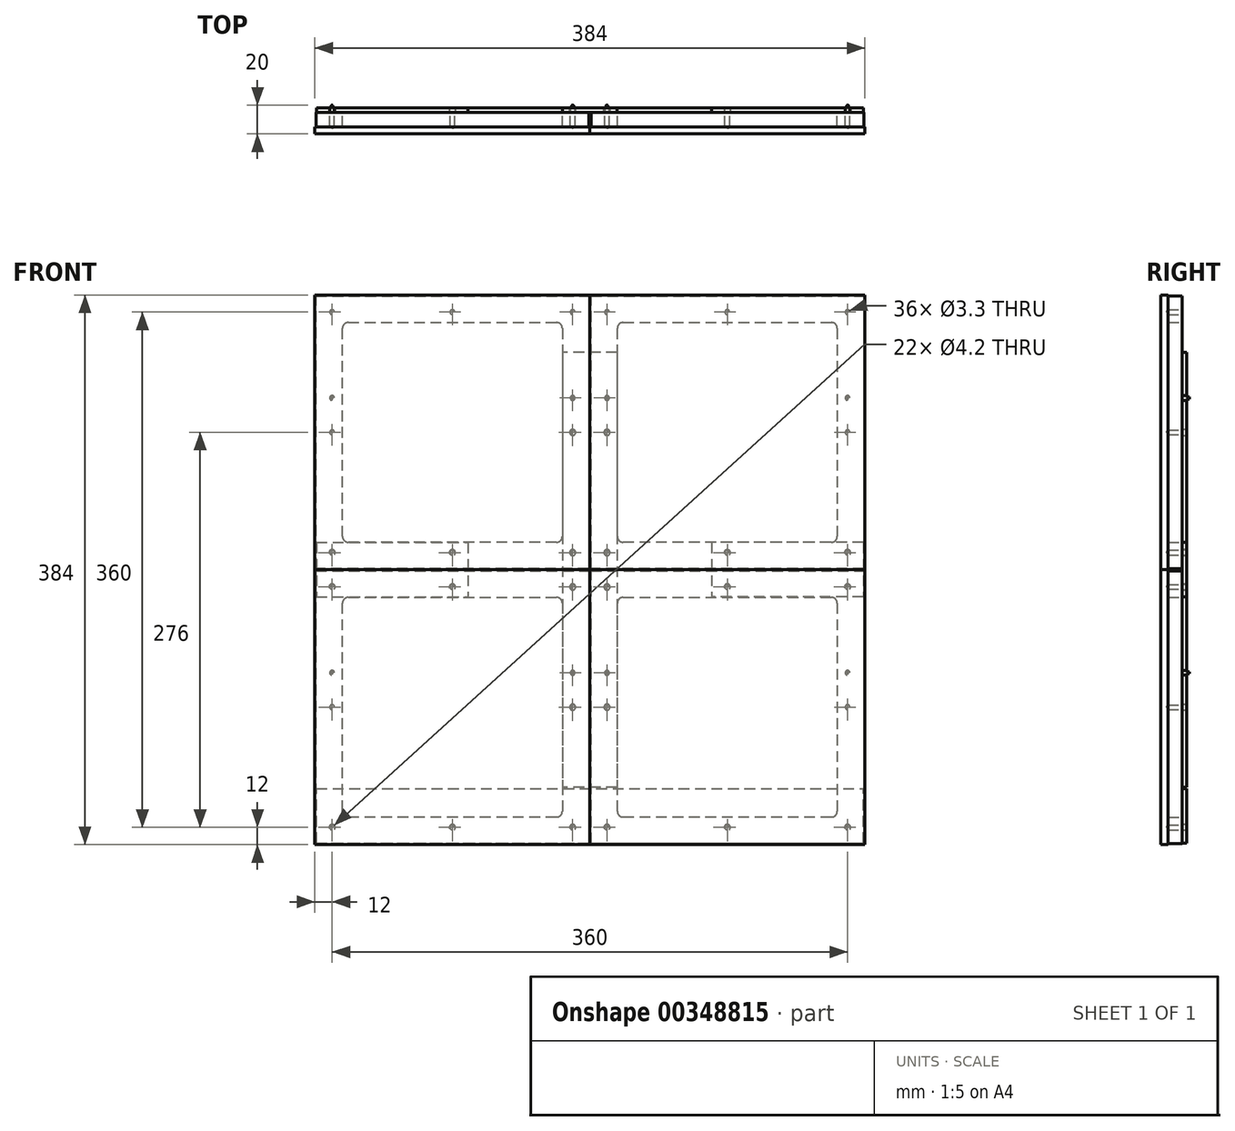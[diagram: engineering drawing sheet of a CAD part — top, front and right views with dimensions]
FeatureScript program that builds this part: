
annotation { "Feature Type Name" : "Feature", "Feature Type Description" : "" }
export const myFeature = defineFeature(function(context is Context, id is Id, definition is map)
    precondition{}
    {
        {
            var Q0;
            Q0=qCreatedBy(makeId("Front.planeOp"),FACE);
            var sketch = newSketch(context, id + "F0", { "sketchPlane" : qUnion([Q0])});
            skLineSegment(sketch, "E0.bottom", {"start": v(-96, -96) * mm, "end": v(96, -96) * mm});
            skLineSegment(sketch, "E0.top", {"start": v(-96, 96) * mm, "end": v(96, 96) * mm});
            skLineSegment(sketch, "E0.left", {"start": v(-96, -96) * mm, "end": v(-96, 96) * mm});
            skLineSegment(sketch, "E0.right", {"start": v(96, -96) * mm, "end": v(96, 96) * mm});
            skPoint(sketch, "E0.middle", {"position": v(0, 0) * mm});
            skSolve(sketch);
        }
        {
            var Q0;
            Q0 = qSketchRegion(id + "F0", true);
            extrude(context, id + "F1", {"entities" : qUnion([Q0]), "depth" : 15 * mm});
        }
        {
            var Q0;
            Q0=qCreatedBy(makeId("Front.planeOp"),FACE);
            var sketch = newSketch(context, id + "F2", { "sketchPlane" : qUnion([Q0])});
            skLineSegment(sketch, "E1.0.0", {"start": v(-96, 96) * mm, "end": v(96, 96) * mm});
            skLineSegment(sketch, "E1.0.1", {"start": v(96, 96) * mm, "end": v(96, -96) * mm});
            skLineSegment(sketch, "E1.0.2", {"start": v(96, -96) * mm, "end": v(-96, -96) * mm});
            skLineSegment(sketch, "E1.0.3", {"start": v(-96, -96) * mm, "end": v(-96, 96) * mm});
            skLineSegment(sketch, "E2.0", {"start": v(-95.25, 95.25) * mm, "end": v(95.25, 95.25) * mm});
            skLineSegment(sketch, "E2.1", {"start": v(-95.25, -95.25) * mm, "end": v(-95.25, 95.25) * mm});
            skLineSegment(sketch, "E2.2", {"start": v(95.25, -95.25) * mm, "end": v(-95.25, -95.25) * mm});
            skLineSegment(sketch, "E2.3", {"start": v(95.25, 95.25) * mm, "end": v(95.25, -95.25) * mm});
            skSolve(sketch);
        }
        {
            var Q0;
            Q0 = qSketchRegion(id + "F2", true);
            extrude(context, id + "F3", {"entities" : qUnion([Q0]), "operationType" : NewBodyOperationType.REMOVE, "depth" : 10 * mm});
        }
        {
            var Q0;
            Q0=makeQuery(id+"F1.opExtrude","CAP_FACE",FACE,{"disambiguationData":[OSD([sQuery(id+"F0.wireOp",EDGE,"E0.bottom"),sQuery(id+"F0.wireOp",EDGE,"E0.top"),sQuery(id+"F0.wireOp",EDGE,"E0.left"),sQuery(id+"F0.wireOp",EDGE,"E0.right")])],"isStart":true});
            var sketch = newSketch(context, id + "F4", { "sketchPlane" : qUnion([Q0])});
            skLineSegment(sketch, "E3.0", {"start": v(72.75, 76.75) * mm, "end": v(-72.75, 76.75) * mm});
            skLineSegment(sketch, "E3.1", {"start": v(76.75, -72.75) * mm, "end": v(76.75, 72.75) * mm});
            skLineSegment(sketch, "E3.2", {"start": v(-72.75, -76.75) * mm, "end": v(72.75, -76.75) * mm});
            skLineSegment(sketch, "E3.3", {"start": v(-76.75, 72.75) * mm, "end": v(-76.75, -72.75) * mm});
            skPoint(sketch, "E4.visualSharp", {"position": v(76.75, 76.75) * mm});
            skArc(sketch, "E4.filletArc", {"start": v(76.75, 72.75) * mm, "mid": v(75.58, 75.58) * mm, "end": v(72.75, 76.75) * mm});
            skPoint(sketch, "E5.visualSharp", {"position": v(76.75, -76.75) * mm});
            skArc(sketch, "E5.filletArc", {"start": v(72.75, -76.75) * mm, "mid": v(75.58, -75.58) * mm, "end": v(76.75, -72.75) * mm});
            skPoint(sketch, "E6.visualSharp", {"position": v(-76.75, -76.75) * mm});
            skArc(sketch, "E6.filletArc", {"start": v(-76.75, -72.75) * mm, "mid": v(-75.58, -75.58) * mm, "end": v(-72.75, -76.75) * mm});
            skPoint(sketch, "E7.visualSharp", {"position": v(-76.75, 76.75) * mm});
            skArc(sketch, "E7.filletArc", {"start": v(-72.75, 76.75) * mm, "mid": v(-75.58, 75.58) * mm, "end": v(-76.75, 72.75) * mm});
            skLineSegment(sketch, "E8.0.0", {"start": v(95.25, 95.25) * mm, "end": v(-95.25, 95.25) * mm, "construction": true});
            skLineSegment(sketch, "E8.0.1", {"start": v(-95.25, 95.25) * mm, "end": v(-95.25, -95.25) * mm, "construction": true});
            skLineSegment(sketch, "E8.0.2", {"start": v(-95.25, -95.25) * mm, "end": v(95.25, -95.25) * mm, "construction": true});
            skLineSegment(sketch, "E8.0.3", {"start": v(95.25, -95.25) * mm, "end": v(95.25, 95.25) * mm, "construction": true});
            skSolve(sketch);
        }
        {
            var Q0;
            Q0=makeQuery(id+"F4.imprint","IMPRINT",FACE,{"disambiguationData":[TD([[makeQuery(id+"F4.imprint","IMPRINT",EDGE,{"derivedFrom":sQuery(id+"F4.wireOp",EDGE,"E3.0")}),1.0]])]});
            extrude(context, id + "F5", {"entities" : qUnion([Q0]), "operationType" : NewBodyOperationType.REMOVE, "oppositeDirection" : true, "depth" : 10 * mm});
        }
        {
            var Q0;
            Q0=makeQuery(id+"F1.opExtrude","CAP_FACE",FACE,{"disambiguationData":[OSD([sQuery(id+"F0.wireOp",EDGE,"E0.bottom"),sQuery(id+"F0.wireOp",EDGE,"E0.top"),sQuery(id+"F0.wireOp",EDGE,"E0.left"),sQuery(id+"F0.wireOp",EDGE,"E0.right")])],"isStart":true});
            var sketch = newSketch(context, id + "F6", { "sketchPlane" : qUnion([Q0])});
            skPoint(sketch, "E9", {"position": v(-84, 84) * mm});
            skPoint(sketch, "E10", {"position": v(0, 84) * mm});
            skPoint(sketch, "E11", {"position": v(84, 84) * mm});
            skPoint(sketch, "E12", {"position": v(84, 0) * mm});
            skPoint(sketch, "E13", {"position": v(84, -84) * mm});
            skPoint(sketch, "E14", {"position": v(0, -84) * mm});
            skPoint(sketch, "E15", {"position": v(-84, -84) * mm});
            skPoint(sketch, "E16", {"position": v(-84, 0) * mm});
            skLineSegment(sketch, "E17", {"start": v(0, 0) * mm, "end": v(95.25, 95.25) * mm, "construction": true});
            skSolve(sketch);
        }
        {
            var Q0;
            Q0=sQuery(id+"F6.wireOp",VERTEX,"E9");
            var Q1;
            Q1=sQuery(id+"F6.wireOp",VERTEX,"E16");
            var Q2;
            Q2=sQuery(id+"F6.wireOp",VERTEX,"E15");
            var Q3;
            Q3=sQuery(id+"F6.wireOp",VERTEX,"E14");
            var Q4;
            Q4=sQuery(id+"F6.wireOp",VERTEX,"E13");
            var Q5;
            Q5=sQuery(id+"F6.wireOp",VERTEX,"E12");
            var Q6;
            Q6=sQuery(id+"F6.wireOp",VERTEX,"E11");
            var Q7;
            Q7=sQuery(id+"F6.wireOp",VERTEX,"E10");
            var Q8;
            Q8=makeQuery(id+"F1.opExtrude","SWEPT_BODY",BODY,{"disambiguationData":[OSD([sQuery(id+"F0.wireOp",EDGE,"E0.bottom"),sQuery(id+"F0.wireOp",EDGE,"E0.top"),sQuery(id+"F0.wireOp",EDGE,"E0.left"),sQuery(id+"F0.wireOp",EDGE,"E0.right")])]});
            hole(context, id + "F7", {"style" : HoleStyle.SIMPLE, "endStyle" : HoleEndStyle.BLIND, "standardTappedOrClearance" : lookupTablePath({ "standard" : "ISO", "engagement" : "75%", "pitch" : "0.7 mm", "size" : "M4", "type" : "Tapped" }), "standardBlindInLast" : lookupTablePath({ "standard" : "ISO", "engagement" : "75%", "pitch" : "0.7 mm", "size" : "M4", "type" : "Tapped" }), "holeDiameter" : 3.3 * mm, "showTappedDepth" : true, "holeDepth" : 10.1 * mm, "tappedDepth" : 8 * mm, "tapClearance" : 3, "locations" : qUnion([Q0, Q1, Q2, Q3, Q4, Q5, Q6, Q7]), "scope" : qUnion([Q8]), "majorDiameter" : 4 * mm});
        }
        {
            var Q0;
            Q0=qCreatedBy(makeId("Front.planeOp"),FACE);
            var sketch = newSketch(context, id + "F8", { "sketchPlane" : qUnion([Q0])});
            skCircle(sketch, "E18", {"center": v(84, 24) * mm, "radius": 1.65 * mm});
            skCircle(sketch, "E19.MirrorC", {"center": v(-84, 24) * mm, "radius": 1.65 * mm});
            skSolve(sketch);
        }
        {
            var Q0;
            Q0 = qSketchRegion(id + "F8", true);
            extrude(context, id + "F9", {"entities" : qUnion([Q0]), "operationType" : NewBodyOperationType.ADD, "oppositeDirection" : true, "depth" : 5 * mm});
        }
        {
            var Q0;
            Q0=makeQuery(id+"F9.opExtrude","CAP_EDGE",EDGE,{"disambiguationData":[OSD([sQuery(id+"F8.wireOp",EDGE,"E18")])],"isStart":false});
            var Q1;
            Q1=makeQuery(id+"F9.opExtrude","CAP_EDGE",EDGE,{"disambiguationData":[OSD([sQuery(id+"F8.wireOp",EDGE,"E19.MirrorC")])],"isStart":false});
            fillet(context, id + "F10", {"entities" : qUnion([Q0, Q1]), "radius" : 1 * mm, "tangentPropagation" : true, "allowEdgeOverflow" : false});
        }
        {
            var Q0;
            Q0=makeQuery(id+"F1.opExtrude","SWEPT_BODY",BODY,{"disambiguationData":[OSD([sQuery(id+"F0.wireOp",EDGE,"E0.bottom"),sQuery(id+"F0.wireOp",EDGE,"E0.top"),sQuery(id+"F0.wireOp",EDGE,"E0.left"),sQuery(id+"F0.wireOp",EDGE,"E0.right")])]});
            transform(context, id + "F11", {"entities" : qUnion([Q0]), "transformType" : TransformType.TRANSLATION_3D, "dx" : 192 * mm, "dy" : 0 * mm, "dz" : 192 * mm, "makeCopy" : true});
        }
        {
            var Q0;
            Q0=makeQuery(id+"F1.opExtrude","SWEPT_BODY",BODY,{"disambiguationData":[OSD([sQuery(id+"F0.wireOp",EDGE,"E0.bottom"),sQuery(id+"F0.wireOp",EDGE,"E0.top"),sQuery(id+"F0.wireOp",EDGE,"E0.left"),sQuery(id+"F0.wireOp",EDGE,"E0.right")])]});
            transform(context, id + "F12", {"entities" : qUnion([Q0]), "transformType" : TransformType.TRANSLATION_3D, "dx" : 0 * mm, "dy" : 0 * mm, "dz" : 192 * mm, "makeCopy" : true});
        }
        {
            var Q0;
            Q0=makeQuery(id+"F1.opExtrude","SWEPT_BODY",BODY,{"disambiguationData":[OSD([sQuery(id+"F0.wireOp",EDGE,"E0.bottom"),sQuery(id+"F0.wireOp",EDGE,"E0.top"),sQuery(id+"F0.wireOp",EDGE,"E0.left"),sQuery(id+"F0.wireOp",EDGE,"E0.right")])]});
            transform(context, id + "F13", {"entities" : qUnion([Q0]), "transformType" : TransformType.TRANSLATION_3D, "dx" : 192 * mm, "dy" : 0 * mm, "dz" : 0 * mm, "makeCopy" : true});
        }
        {
            var Q0;
            Q0=qCreatedBy(makeId("Front.planeOp"),FACE);
            var sketch = newSketch(context, id + "F14", { "sketchPlane" : qUnion([Q0])});
            skLineSegment(sketch, "E20.bottom", {"start": v(115.05, 248) * mm, "end": v(76.95, 248) * mm});
            skLineSegment(sketch, "E20.top", {"start": v(115.05, -56) * mm, "end": v(76.95, -56) * mm});
            skLineSegment(sketch, "E20.left", {"start": v(115.05, 248) * mm, "end": v(115.05, -56) * mm});
            skLineSegment(sketch, "E20.right", {"start": v(76.95, 248) * mm, "end": v(76.95, -56) * mm});
            skPoint(sketch, "E21", {"position": v(96, 96) * mm});
            skPoint(sketch, "E21.positionSnap0", {"position": v(96, 248) * mm});
            skPoint(sketch, "E21.positionSnap1", {"position": v(76.95, 96) * mm});
            skSolve(sketch);
        }
        {
            var Q0;
            Q0 = qSketchRegion(id + "F14", true);
            extrude(context, id + "F15", {"entities" : qUnion([Q0]), "oppositeDirection" : true, "depth" : 3.17 * mm});
        }
        {
            var Q0;
            Q0=makeQuery(id+"F15.opExtrude","CAP_FACE",FACE,{"disambiguationData":[OSD([sQuery(id+"F14.wireOp",EDGE,"E20.bottom"),sQuery(id+"F14.wireOp",EDGE,"E20.top"),sQuery(id+"F14.wireOp",EDGE,"E20.left"),sQuery(id+"F14.wireOp",EDGE,"E20.right")])],"isStart":false});
            var sketch = newSketch(context, id + "F16", { "sketchPlane" : qUnion([Q0])});
            skLineSegment(sketch, "E22", {"start": v(-96, -56) * mm, "end": v(-96, 248) * mm, "construction": true});
            skLineSegment(sketch, "E23", {"start": v(-76.95, 96) * mm, "end": v(-115.05, 96) * mm, "construction": true});
            skPoint(sketch, "E24", {"position": v(-84, 84) * mm});
            skPoint(sketch, "E25", {"position": v(-84, 0) * mm});
            skPoint(sketch, "E26.MirrorP", {"position": v(-108, 0) * mm});
            skPoint(sketch, "E27.MirrorP", {"position": v(-108, 84) * mm});
            skPoint(sketch, "E28.MirrorP", {"position": v(-108, 108) * mm});
            skPoint(sketch, "E29.MirrorP", {"position": v(-84, 108) * mm});
            skPoint(sketch, "E30.MirrorP", {"position": v(-108, 192) * mm});
            skPoint(sketch, "E31.MirrorP", {"position": v(-84, 192) * mm});
            skCircle(sketch, "E32.0", {"center": v(-84, 216) * mm, "radius": 0.65 * mm, "construction": true});
            skCircle(sketch, "E33.0", {"center": v(-84, 24) * mm, "radius": 1.65 * mm, "construction": true});
            skPoint(sketch, "E34.MirrorP", {"position": v(-108, 24) * mm});
            skPoint(sketch, "E35.MirrorP", {"position": v(-108, 216) * mm});
            skSolve(sketch);
        }
        {
            var Q0;
            Q0=sQuery(id+"F16.wireOp",VERTEX,"E29.MirrorP");
            var Q1;
            Q1=sQuery(id+"F16.wireOp",VERTEX,"E31.MirrorP");
            var Q2;
            Q2=sQuery(id+"F16.wireOp",VERTEX,"E30.MirrorP");
            var Q3;
            Q3=sQuery(id+"F16.wireOp",VERTEX,"E28.MirrorP");
            var Q4;
            Q4=sQuery(id+"F16.wireOp",VERTEX,"E27.MirrorP");
            var Q5;
            Q5=sQuery(id+"F16.wireOp",VERTEX,"E26.MirrorP");
            var Q6;
            Q6=sQuery(id+"F16.wireOp",VERTEX,"E25");
            var Q7;
            Q7=sQuery(id+"F16.wireOp",VERTEX,"E24");
            var Q8;
            Q8=makeQuery(id+"F15.opExtrude","SWEPT_BODY",BODY,{"disambiguationData":[OSD([sQuery(id+"F14.wireOp",EDGE,"E20.bottom"),sQuery(id+"F14.wireOp",EDGE,"E20.top"),sQuery(id+"F14.wireOp",EDGE,"E20.left"),sQuery(id+"F14.wireOp",EDGE,"E20.right")])]});
            hole(context, id + "F17", {"style" : HoleStyle.SIMPLE, "endStyle" : HoleEndStyle.THROUGH, "standardTappedOrClearance" : lookupTablePath({ "standard" : "ISO", "fit" : "Close", "size" : "M4", "type" : "Clearance" }), "standardBlindInLast" : lookupTablePath({ "fit" : "Close", "standard" : "ISO", "size" : "M4", "type" : "Clearance" }), "holeDiameter" : 4.2 * mm, "tappedDepth" : 8 * mm, "tapClearance" : 3, "locations" : qUnion([Q0, Q1, Q2, Q3, Q4, Q5, Q6, Q7]), "scope" : qUnion([Q8])});
        }
        {
            var Q0;
            Q0=sQuery(id+"F16.wireOp",VERTEX,"E35.MirrorP");
            var Q1;
            Q1=sQuery(id+"F16.wireOp",VERTEX,"E32.0.center");
            var Q2;
            Q2=sQuery(id+"F16.wireOp",VERTEX,"E34.MirrorP");
            var Q3;
            Q3=sQuery(id+"F16.wireOp",VERTEX,"E33.0.center");
            var Q4;
            Q4=makeQuery(id+"F15.opExtrude","SWEPT_BODY",BODY,{"disambiguationData":[OSD([sQuery(id+"F14.wireOp",EDGE,"E20.bottom"),sQuery(id+"F14.wireOp",EDGE,"E20.top"),sQuery(id+"F14.wireOp",EDGE,"E20.left"),sQuery(id+"F14.wireOp",EDGE,"E20.right")])]});
            hole(context, id + "F18", {"style" : HoleStyle.SIMPLE, "endStyle" : HoleEndStyle.THROUGH, "standardTappedOrClearance" : lookupTablePath({ "standard" : "ISO", "fit" : "Normal", "size" : "M3", "type" : "Clearance" }), "standardBlindInLast" : lookupTablePath({ "fit" : "Standard", "standard" : "ISO", "size" : "M3", "type" : "Clearance" }), "holeDiameter" : 3.3 * mm, "tappedDepth" : 8 * mm, "tapClearance" : 3, "locations" : qUnion([Q0, Q1, Q2, Q3]), "scope" : qUnion([Q4])});
        }
        {
            var Q0;
            Q0=qCreatedBy(makeId("Front.planeOp"),FACE);
            var sketch = newSketch(context, id + "F19", { "sketchPlane" : qUnion([Q0])});
            skCircle(sketch, "E36.0", {"center": v(0, 84) * mm, "radius": 1.65 * mm, "construction": true});
            skCircle(sketch, "E37.0", {"center": v(-84, 84) * mm, "radius": 1.65 * mm, "construction": true});
            skLineSegment(sketch, "E38.0", {"start": v(-96, 96) * mm, "end": v(96, 96) * mm, "construction": true});
            skLineSegment(sketch, "E39.bottom", {"start": v(-95, 115.05) * mm, "end": v(11, 115.05) * mm});
            skLineSegment(sketch, "E39.top", {"start": v(-95, 76.95) * mm, "end": v(11, 76.95) * mm});
            skLineSegment(sketch, "E39.left", {"start": v(-95, 115.05) * mm, "end": v(-95, 76.95) * mm});
            skLineSegment(sketch, "E39.right", {"start": v(11, 115.05) * mm, "end": v(11, 76.95) * mm});
            skPoint(sketch, "E40.MirrorP", {"position": v(0, 108) * mm});
            skPoint(sketch, "E41.MirrorP", {"position": v(-84, 108) * mm});
            skLineSegment(sketch, "E42", {"start": v(-84, 108) * mm, "end": v(0, 108) * mm, "construction": true});
            skLineSegment(sketch, "E43", {"start": v(-42, 108) * mm, "end": v(-42, 84.08) * mm, "construction": true});
            skLineSegment(sketch, "E44.0", {"start": v(-96, -96) * mm, "end": v(-96, 96) * mm, "construction": true});
            skSolve(sketch);
        }
        {
            var Q0;
            Q0 = qSketchRegion(id + "F19", true);
            extrude(context, id + "F20", {"entities" : qUnion([Q0]), "oppositeDirection" : true, "depth" : 3.17 * mm});
        }
        {
            var Q0;
            Q0=sQuery(id+"F19.wireOp",VERTEX,"E36.0.center");
            var Q1;
            Q1=sQuery(id+"F19.wireOp",VERTEX,"E40.MirrorP");
            var Q2;
            Q2=sQuery(id+"F19.wireOp",VERTEX,"E41.MirrorP");
            var Q3;
            Q3=sQuery(id+"F19.wireOp",VERTEX,"E37.0.center");
            var Q4;
            Q4=makeQuery(id+"F20.opExtrude","SWEPT_BODY",BODY,{"disambiguationData":[OSD([sQuery(id+"F19.wireOp",EDGE,"E39.bottom"),sQuery(id+"F19.wireOp",EDGE,"E39.top"),sQuery(id+"F19.wireOp",EDGE,"E39.left"),sQuery(id+"F19.wireOp",EDGE,"E39.right")])]});
            hole(context, id + "F21", {"style" : HoleStyle.SIMPLE, "endStyle" : HoleEndStyle.THROUGH, "standardTappedOrClearance" : lookupTablePath({ "standard" : "ISO", "fit" : "Close", "size" : "M4", "type" : "Clearance" }), "standardBlindInLast" : lookupTablePath({ "fit" : "Close", "standard" : "ISO", "size" : "M4", "type" : "Clearance" }), "holeDiameter" : 4.2 * mm, "tappedDepth" : 8 * mm, "tapClearance" : 3, "locations" : qUnion([Q0, Q1, Q2, Q3]), "scope" : qUnion([Q4])});
        }
        {
            var Q0;
            Q0=makeQuery(id+"F20.opExtrude","SWEPT_BODY",BODY,{"disambiguationData":[OSD([sQuery(id+"F19.wireOp",EDGE,"E39.bottom"),sQuery(id+"F19.wireOp",EDGE,"E39.top"),sQuery(id+"F19.wireOp",EDGE,"E39.left"),sQuery(id+"F19.wireOp",EDGE,"E39.right")])]});
            var Q1;
            Q1=makeQuery(id+"F1.opExtrude","SWEPT_FACE",FACE,{"disambiguationData":[OSD([sQuery(id+"F0.wireOp",EDGE,"E0.right")])]});
            mirror(context, id + "F22", {"entities" : qUnion([Q0]), "mirrorPlane" : qUnion([Q1])});
        }
        {
            var Q0;
            Q0=qCreatedBy(makeId("Front.planeOp"),FACE);
            var sketch = newSketch(context, id + "F23", { "sketchPlane" : qUnion([Q0])});
            skCircle(sketch, "E45.0", {"center": v(84, -84) * mm, "radius": 1.65 * mm, "construction": true});
            skCircle(sketch, "E46.0", {"center": v(0, -84) * mm, "radius": 1.65 * mm, "construction": true});
            skCircle(sketch, "E47.0", {"center": v(-84, -84) * mm, "radius": 1.65 * mm, "construction": true});
            skLineSegment(sketch, "E48.0", {"start": v(-96, -96) * mm, "end": v(-96, -36.88) * mm, "construction": true});
            skLineSegment(sketch, "E49.0", {"start": v(96, -96) * mm, "end": v(96, -30.84) * mm, "construction": true});
            skLineSegment(sketch, "E50.bottom", {"start": v(-95, -95) * mm, "end": v(287, -95) * mm});
            skLineSegment(sketch, "E50.top", {"start": v(-95, -56.9) * mm, "end": v(287, -56.9) * mm});
            skLineSegment(sketch, "E50.left", {"start": v(-95, -95) * mm, "end": v(-95, -56.9) * mm});
            skLineSegment(sketch, "E50.right", {"start": v(287, -95) * mm, "end": v(287, -56.9) * mm});
            skPoint(sketch, "E51.MirrorP", {"position": v(276, -84) * mm});
            skPoint(sketch, "E52.MirrorP", {"position": v(192, -84) * mm});
            skPoint(sketch, "E53.MirrorP", {"position": v(108, -84) * mm});
            skLineSegment(sketch, "E54.0", {"start": v(96, -96) * mm, "end": v(-96, -96) * mm, "construction": true});
            skSolve(sketch);
        }
        {
            var Q0;
            Q0 = qSketchRegion(id + "F23", true);
            extrude(context, id + "F24", {"entities" : qUnion([Q0]), "oppositeDirection" : true, "depth" : 3.17 * mm});
        }
        {
            var Q0;
            Q0=sQuery(id+"F23.wireOp",VERTEX,"E47.0.center");
            var Q1;
            Q1=sQuery(id+"F23.wireOp",VERTEX,"E46.0.center");
            var Q2;
            Q2=sQuery(id+"F23.wireOp",VERTEX,"E45.0.center");
            var Q3;
            Q3=sQuery(id+"F23.wireOp",VERTEX,"E53.MirrorP");
            var Q4;
            Q4=sQuery(id+"F23.wireOp",VERTEX,"E52.MirrorP");
            var Q5;
            Q5=sQuery(id+"F23.wireOp",VERTEX,"E51.MirrorP");
            var Q6;
            Q6=makeQuery(id+"F24.opExtrude","SWEPT_BODY",BODY,{"disambiguationData":[OSD([sQuery(id+"F23.wireOp",EDGE,"E50.bottom"),sQuery(id+"F23.wireOp",EDGE,"E50.top"),sQuery(id+"F23.wireOp",EDGE,"E50.left"),sQuery(id+"F23.wireOp",EDGE,"E50.right")])]});
            hole(context, id + "F25", {"style" : HoleStyle.SIMPLE, "endStyle" : HoleEndStyle.THROUGH, "standardTappedOrClearance" : lookupTablePath({ "standard" : "ISO", "fit" : "Close", "size" : "M4", "type" : "Clearance" }), "standardBlindInLast" : lookupTablePath({ "fit" : "Close", "standard" : "ISO", "size" : "M4", "type" : "Clearance" }), "holeDiameter" : 4.2 * mm, "tappedDepth" : 8 * mm, "tapClearance" : 3, "locations" : qUnion([Q0, Q1, Q2, Q3, Q4, Q5]), "scope" : qUnion([Q6])});
        }
    });
